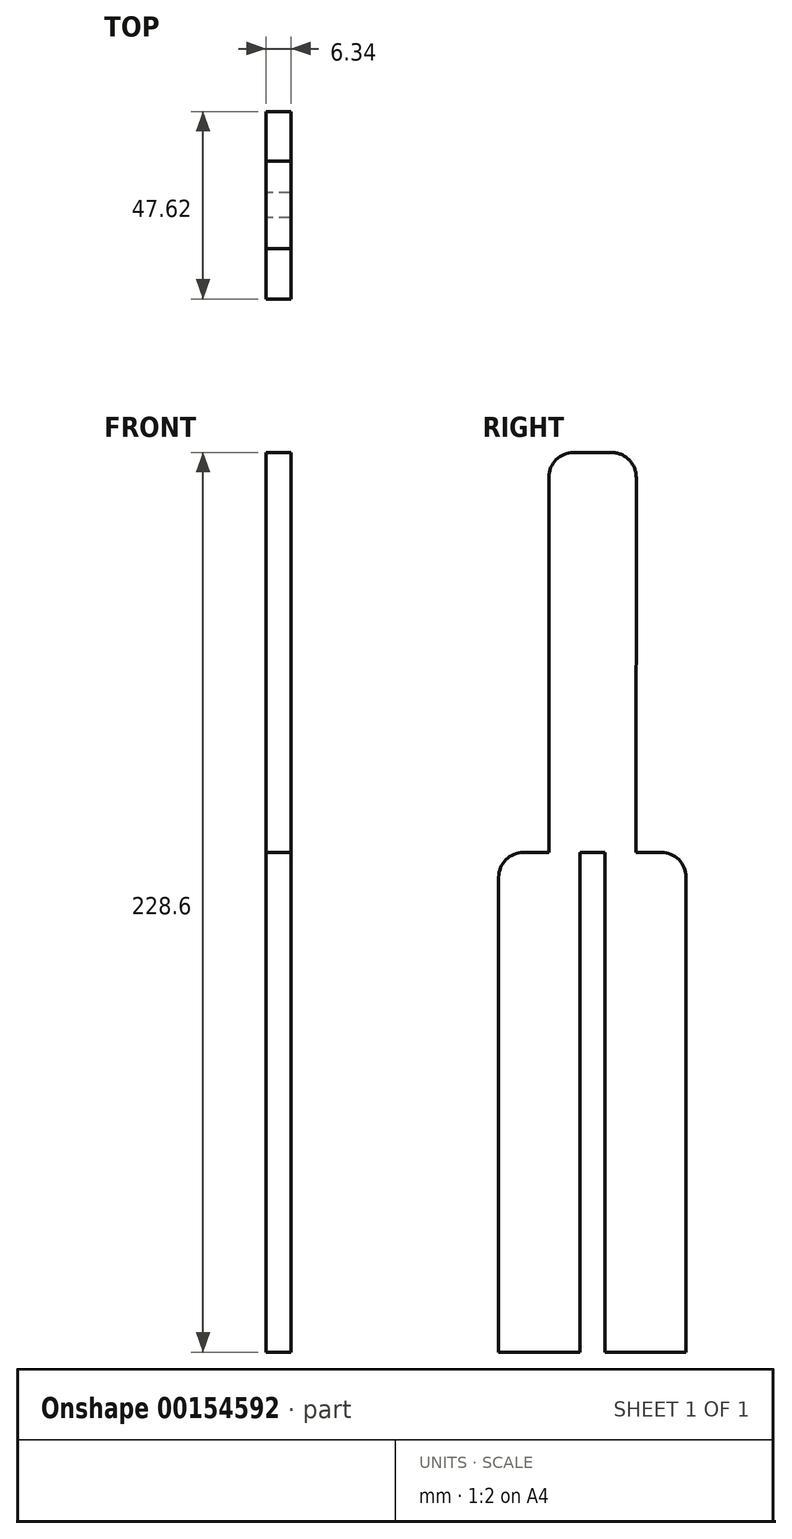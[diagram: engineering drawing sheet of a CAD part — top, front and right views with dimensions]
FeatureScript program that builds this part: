
annotation { "Feature Type Name" : "Feature", "Feature Type Description" : "" }
export const myFeature = defineFeature(function(context is Context, id is Id, definition is map)
    precondition{}
    {
        {
            var Q0;
            Q0=qCreatedBy(makeId("Right.planeOp"),FACE);
            var sketch = newSketch(context, id + "F0", { "sketchPlane" : qUnion([Q0])});
            skLineSegment(sketch, "E0.bottom", {"start": v(23.81, -63.5) * mm, "end": v(3.18, -63.5) * mm});
            skLineSegment(sketch, "E0.top", {"start": v(17.46, 63.5) * mm, "end": v(17.46, 63.5) * mm});
            skLineSegment(sketch, "E0.left", {"start": v(23.81, -63.5) * mm, "end": v(23.81, 57.15) * mm});
            skLineSegment(sketch, "E0.right", {"start": v(-23.81, -63.5) * mm, "end": v(-23.81, 57.15) * mm});
            skPoint(sketch, "E0.middle", {"position": v(0, 0) * mm});
            skLineSegment(sketch, "E1", {"start": v(-11.1, 63.5) * mm, "end": v(-11.1, 158.75) * mm});
            skLineSegment(sketch, "E2", {"start": v(-4.75, 165.1) * mm, "end": v(4.77, 165.1) * mm});
            skLineSegment(sketch, "E3", {"start": v(11.12, 158.75) * mm, "end": v(11.11, 63.5) * mm});
            skLineSegment(sketch, "E4.trimOffspring", {"start": v(-17.45, 63.5) * mm, "end": v(-17.46, 63.5) * mm});
            skPoint(sketch, "E5.start.orphan", {"position": v(0, -63.5) * mm});
            skPoint(sketch, "E6.visualSharp", {"position": v(-11.1, 63.5) * mm});
            skPoint(sketch, "E7.visualSharp", {"position": v(11.11, 63.5) * mm});
            skPoint(sketch, "E8.visualSharp", {"position": v(-23.81, 63.5) * mm});
            skArc(sketch, "E8.filletArc", {"start": v(-17.46, 63.5) * mm, "mid": v(-21.95, 61.64) * mm, "end": v(-23.81, 57.15) * mm});
            skPoint(sketch, "E9.visualSharp", {"position": v(23.81, 63.5) * mm});
            skArc(sketch, "E9.filletArc", {"start": v(23.81, 57.15) * mm, "mid": v(21.95, 61.64) * mm, "end": v(17.46, 63.5) * mm});
            skPoint(sketch, "E10.visualSharp", {"position": v(11.13, 165.1) * mm});
            skArc(sketch, "E10.filletArc", {"start": v(11.12, 158.75) * mm, "mid": v(9.26, 163.24) * mm, "end": v(4.77, 165.1) * mm});
            skPoint(sketch, "E11.visualSharp", {"position": v(-11.1, 165.1) * mm});
            skArc(sketch, "E11.filletArc", {"start": v(-4.75, 165.1) * mm, "mid": v(-9.24, 163.24) * mm, "end": v(-11.1, 158.75) * mm});
            skLineSegment(sketch, "E12", {"start": v(-3.18, -63.5) * mm, "end": v(-3.18, 63.5) * mm});
            skLineSegment(sketch, "E13", {"start": v(-3.18, 63.5) * mm, "end": v(3.17, 63.5) * mm});
            skLineSegment(sketch, "E14", {"start": v(3.17, 63.5) * mm, "end": v(3.17, -63.5) * mm});
            skLineSegment(sketch, "E15.trimOffspring", {"start": v(-3.18, -63.5) * mm, "end": v(-23.81, -63.5) * mm});
            skLineSegment(sketch, "E16", {"start": v(-17.45, 63.5) * mm, "end": v(-11.1, 63.5) * mm});
            skLineSegment(sketch, "E17", {"start": v(11.11, 63.5) * mm, "end": v(17.46, 63.5) * mm});
            skSolve(sketch);
        }
        {
            var Q0;
            Q0 = qSketchRegion(id + "F0", true);
            extrude(context, id + "F1", {"entities" : qUnion([Q0]), "endBound" : BoundingType.SYMMETRIC, "depth" : 6.35 * mm});
        }
    });
